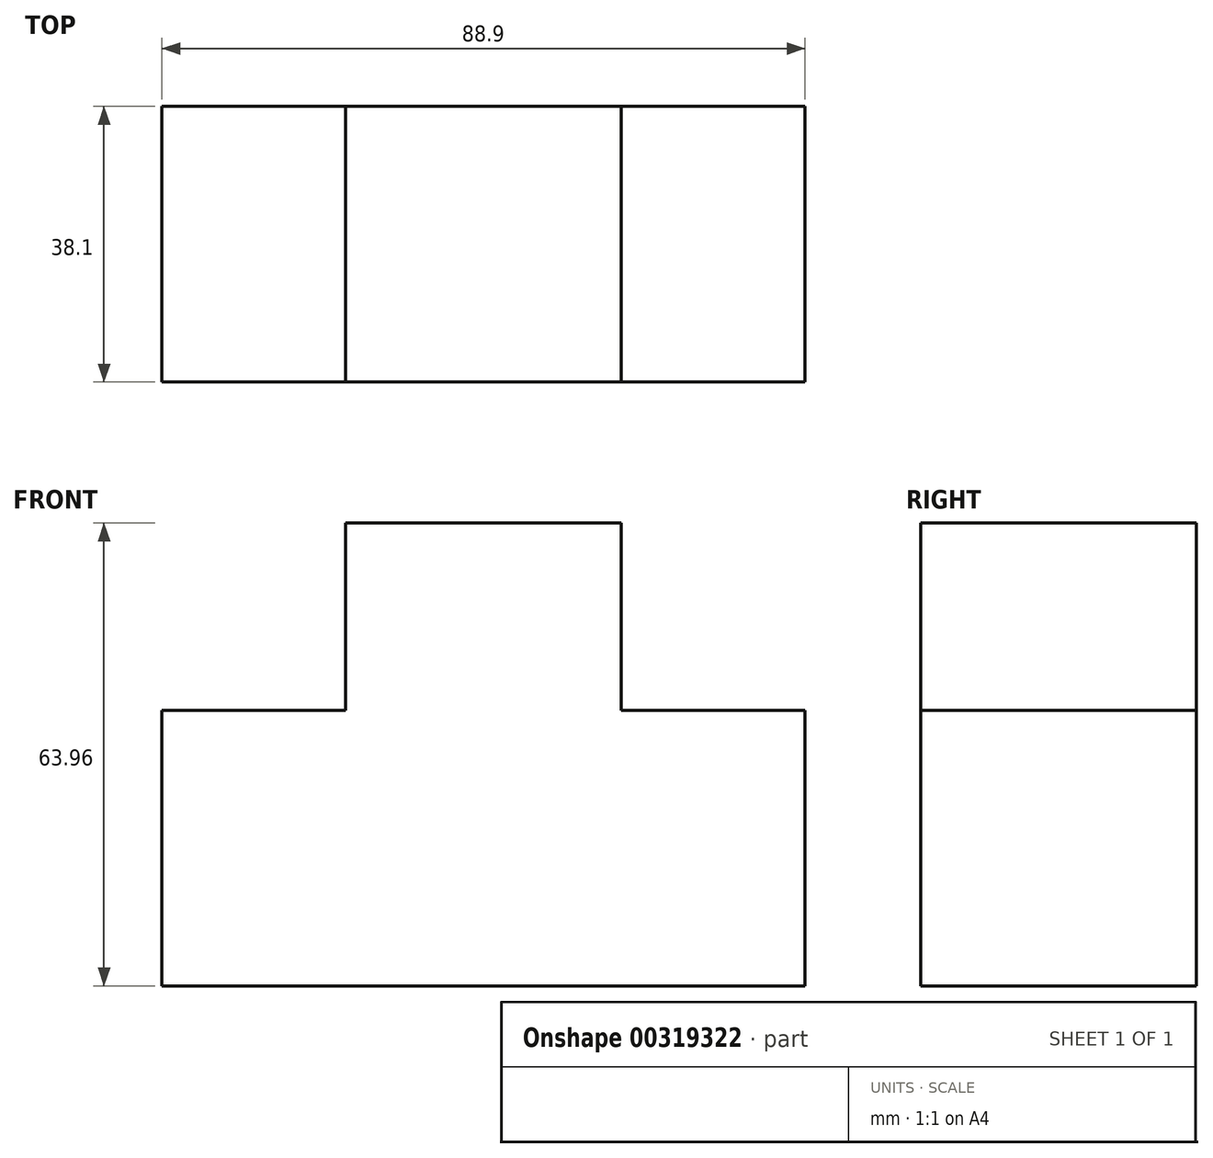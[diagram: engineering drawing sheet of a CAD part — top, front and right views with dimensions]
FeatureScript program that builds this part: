
annotation { "Feature Type Name" : "Feature", "Feature Type Description" : "" }
export const myFeature = defineFeature(function(context is Context, id is Id, definition is map)
    precondition{}
    {
        {
            var Q0;
            Q0=qCreatedBy(makeId("Front.planeOp"),FACE);
            var sketch = newSketch(context, id + "F0", { "sketchPlane" : qUnion([Q0])});
            skLineSegment(sketch, "E0", {"start": v(-46, -38.21) * mm, "end": v(42.9, -38.21) * mm});
            skLineSegment(sketch, "E1", {"start": v(42.9, -38.21) * mm, "end": v(42.9, -0.11) * mm});
            skLineSegment(sketch, "E2", {"start": v(42.9, -0.11) * mm, "end": v(17.5, -0.11) * mm});
            skLineSegment(sketch, "E3", {"start": v(17.5, -0.11) * mm, "end": v(17.5, 25.75) * mm});
            skLineSegment(sketch, "E4", {"start": v(17.5, 25.75) * mm, "end": v(-20.6, 25.75) * mm});
            skLineSegment(sketch, "E5", {"start": v(-20.6, 25.75) * mm, "end": v(-20.6, -0.11) * mm});
            skLineSegment(sketch, "E6", {"start": v(-20.6, -0.11) * mm, "end": v(-46, -0.11) * mm});
            skLineSegment(sketch, "E7", {"start": v(-46, -0.11) * mm, "end": v(-46, -38.21) * mm});
            skSolve(sketch);
        }
        {
            var Q0;
            Q0 = qSketchRegion(id + "F0", true);
            var Q1;
            Q1=makeQuery(id+"F0.imprint","IMPRINT",FACE,{"disambiguationData":[TD([[makeQuery(id+"F0.imprint","IMPRINT",EDGE,{"derivedFrom":sQuery(id+"F0.wireOp",EDGE,"E0")}),1.0]])]});
            extrude(context, id + "F1", {"entities" : qUnion([Q0, Q1]), "depth" : 38.1 * mm});
        }
    });
